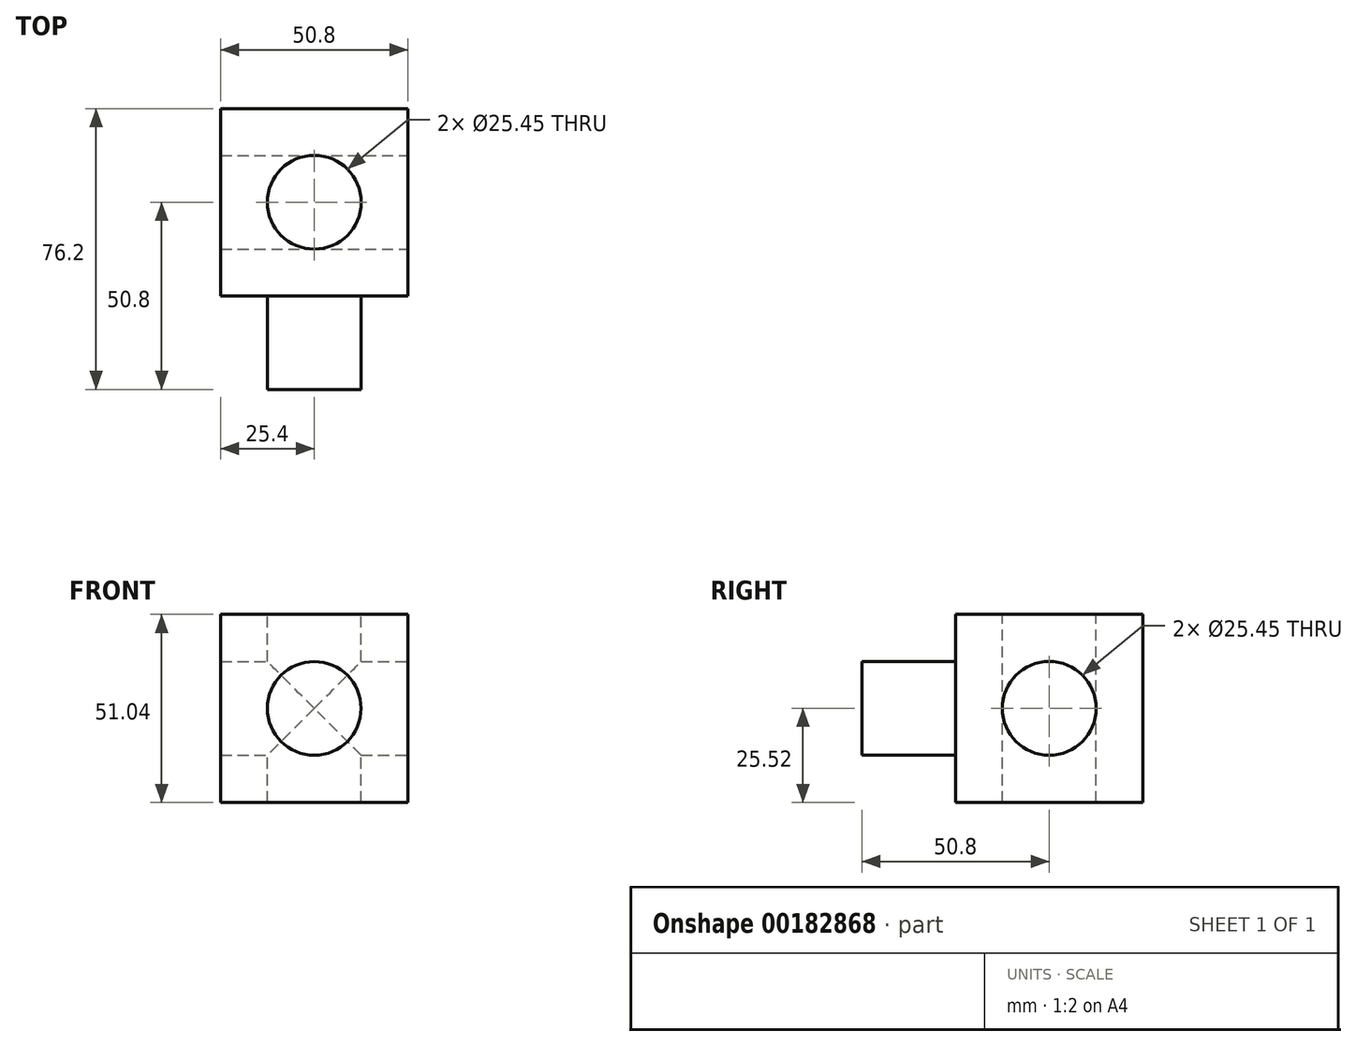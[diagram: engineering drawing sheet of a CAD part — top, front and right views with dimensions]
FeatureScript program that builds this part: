
annotation { "Feature Type Name" : "Feature", "Feature Type Description" : "" }
export const myFeature = defineFeature(function(context is Context, id is Id, definition is map)
    precondition{}
    {
        {
            var Q0;
            Q0=qCreatedBy(makeId("Front.planeOp"),FACE);
            var sketch = newSketch(context, id + "F0", { "sketchPlane" : qUnion([Q0])});
            skLineSegment(sketch, "E0.bottom", {"start": v(25.4, 25.52) * mm, "end": v(-25.4, 25.52) * mm});
            skLineSegment(sketch, "E0.top", {"start": v(25.4, -25.52) * mm, "end": v(-25.4, -25.52) * mm});
            skLineSegment(sketch, "E0.left", {"start": v(25.4, 25.52) * mm, "end": v(25.4, -25.52) * mm});
            skLineSegment(sketch, "E0.right", {"start": v(-25.4, 25.52) * mm, "end": v(-25.4, -25.52) * mm});
            skPoint(sketch, "E0.middle", {"position": v(0, 0) * mm});
            skSolve(sketch);
        }
        {
            var Q0;
            Q0=qCreatedBy(makeId("Front.planeOp"),FACE);
            var sketch = newSketch(context, id + "F1", { "sketchPlane" : qUnion([Q0])});
            skCircle(sketch, "E1", {"center": v(0, 0) * mm, "radius": 12.7 * mm});
            skSolve(sketch);
        }
        {
            var Q0;
            Q0=makeQuery(id+"F1.imprint","IMPRINT",FACE,{"disambiguationData":[TD([[makeQuery(id+"F1.imprint","IMPRINT",EDGE,{"derivedFrom":sQuery(id+"F1.wireOp",EDGE,"E1")}),1.0]])]});
            extrude(context, id + "F2", {"entities" : qUnion([Q0]), "depth" : 25.4 * mm});
        }
        {
            var Q0;
            Q0=makeQuery(id+"F0.imprint","IMPRINT",FACE,{"disambiguationData":[TD([[makeQuery(id+"F0.imprint","IMPRINT",EDGE,{"derivedFrom":sQuery(id+"F0.wireOp",EDGE,"E0.bottom")}),1.0]])]});
            extrude(context, id + "F3", {"entities" : qUnion([Q0]), "operationType" : NewBodyOperationType.ADD, "oppositeDirection" : true, "depth" : 50.8 * mm});
        }
        {
            var Q0;
            Q0=makeQuery(id+"F3.opExtrude","SWEPT_FACE",FACE,{"disambiguationData":[OSD([sQuery(id+"F0.wireOp",EDGE,"E0.left")])]});
            var sketch = newSketch(context, id + "F4", { "sketchPlane" : qUnion([Q0])});
            skPoint(sketch, "E2.centerSnap0", {"position": v(25.4, 25.52) * mm});
            skPoint(sketch, "E3.center.orphan", {"position": v(25.4, 0) * mm});
            skSolve(sketch);
        }
        {
            var Q0;
            Q0=sQuery(id+"F4.wireOp",VERTEX,"E3.center.orphan");
            var Q1;
            Q1=makeQuery(id+"F2.opExtrude","SWEPT_BODY",BODY,{"disambiguationData":[OSD([sQuery(id+"F1.wireOp",EDGE,"E1")])]});
            hole(context, id + "F5", {"style" : HoleStyle.SIMPLE, "endStyle" : HoleEndStyle.THROUGH, "holeDiameter" : 25.45 * mm, "startFromSketch" : true, "locations" : qUnion([Q0]), "scope" : qUnion([Q1]), "isTappedThrough" : true});
        }
        {
            var Q0;
            Q0=makeQuery(id+"F3.opExtrude","SWEPT_FACE",FACE,{"disambiguationData":[OSD([sQuery(id+"F0.wireOp",EDGE,"E0.bottom")])]});
            var sketch = newSketch(context, id + "F6", { "sketchPlane" : qUnion([Q0])});
            skCircle(sketch, "E4", {"center": v(0, 25.4) * mm, "radius": 12.73 * mm});
            skPoint(sketch, "E4.centerSnap0", {"position": v(25.4, 25.4) * mm});
            skSolve(sketch);
        }
        {
            var Q0;
            Q0=sQuery(id+"F6.wireOp",VERTEX,"E4.center");
            var Q1;
            Q1=makeQuery(id+"F2.opExtrude","SWEPT_BODY",BODY,{"disambiguationData":[OSD([sQuery(id+"F1.wireOp",EDGE,"E1")])]});
            hole(context, id + "F7", {"style" : HoleStyle.SIMPLE, "endStyle" : HoleEndStyle.THROUGH, "holeDiameter" : 25.45 * mm, "startFromSketch" : true, "locations" : qUnion([Q0]), "scope" : qUnion([Q1]), "isTappedThrough" : true});
        }
    });
